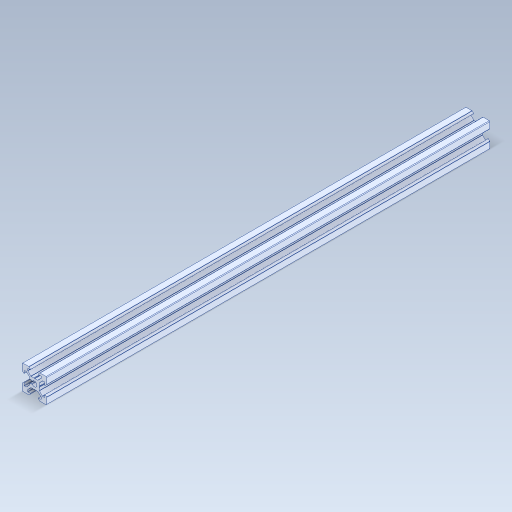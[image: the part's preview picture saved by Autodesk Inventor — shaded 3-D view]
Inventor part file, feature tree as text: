
AUTODESK INVENTOR PART (.ipt)
format: ipt  version: 2023 (Build 270158000, 158)  size: 499,200 bytes
history: mixed  units: in
note: dims shown in document units (in); Inventor stores cm internally (conversion verified against a paired STEP export)
features: other x3, extrude x1, sketch x1, projected_geometry x1, imported_body x1
ambient origin geometry x8: Origin, YZ Plane, XZ Plane, XY Plane, X Axis, Y Axis, Z Axis, Center Point
bodies: Solid1 (imported_parasolid)
feature tree (7):
  other  "Annotations"
  other  "Boss-Extrude1"
  extrude  "Extrusion1"  Depth=0.106in
  sketch  "Sketch2"  dims[d5=3.0748in d6=0.0in d0=0.106in d1=0.114in d2=17.3228in]
  projected_geometry  "Projected Loop1"
  other  "Linear Dimension 1"
  imported_body  NMx_Import_Brep_tag  [imported B-rep: ~114 faces, bbox_mm=[20.0, 20.0, 361.9]]
